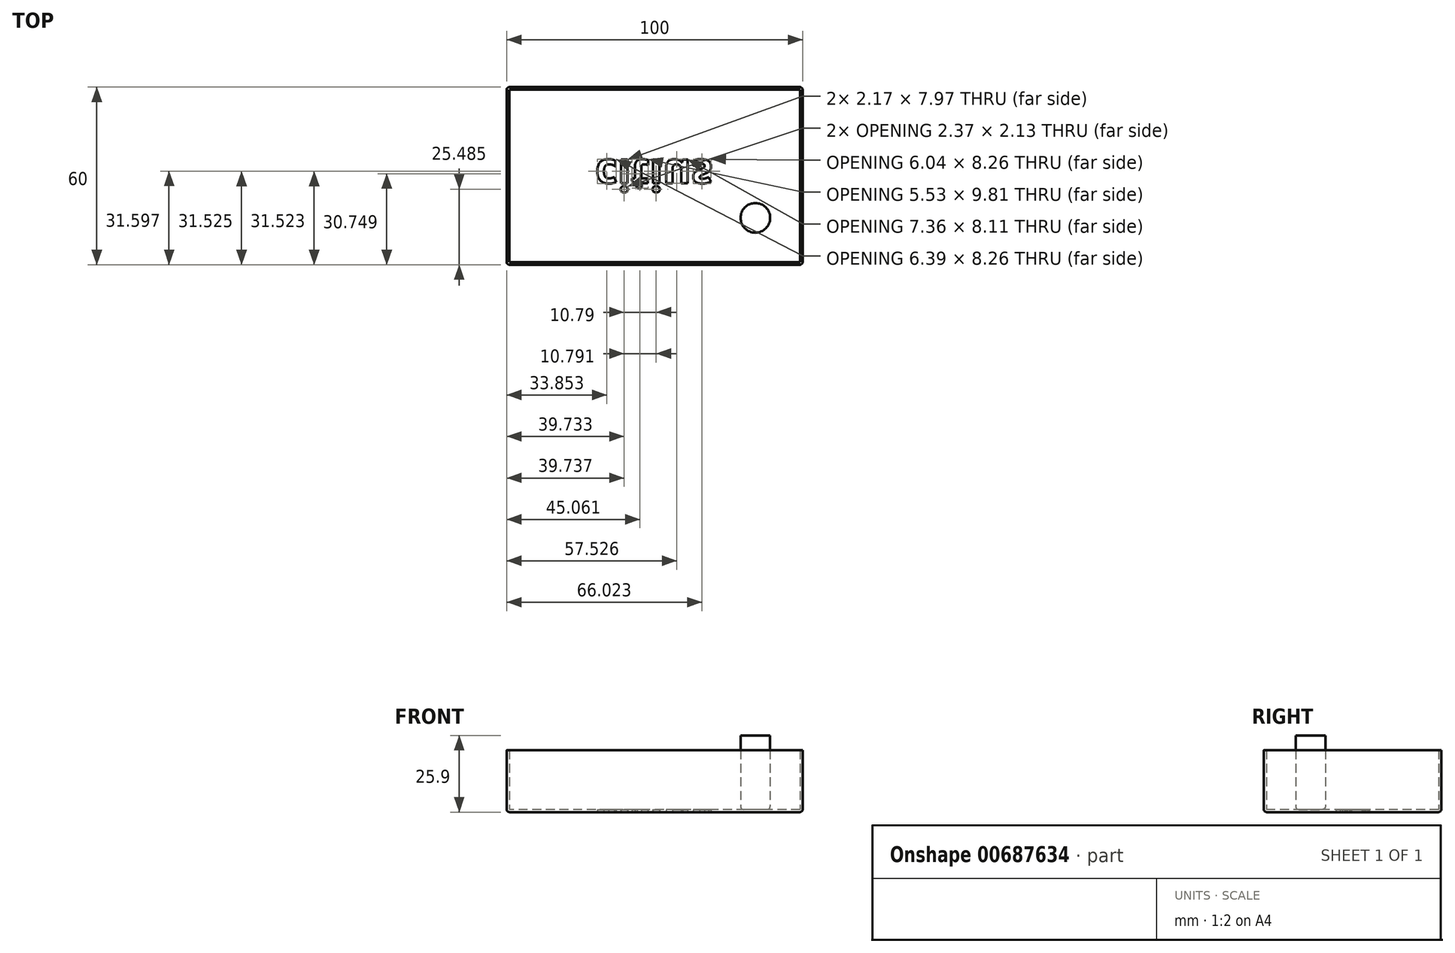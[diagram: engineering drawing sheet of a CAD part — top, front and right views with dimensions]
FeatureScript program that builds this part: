
annotation { "Feature Type Name" : "Feature", "Feature Type Description" : "" }
export const myFeature = defineFeature(function(context is Context, id is Id, definition is map)
    precondition{}
    {
        {
            var Q0;
            Q0=qCreatedBy(makeId("Top.planeOp"),FACE);
            var sketch = newSketch(context, id + "F0", { "sketchPlane" : qUnion([Q0])});
            skLineSegment(sketch, "E0.bottom", {"start": v(-47.64, 21.7) * mm, "end": v(52.36, 21.7) * mm});
            skLineSegment(sketch, "E0.top", {"start": v(-47.64, -38.3) * mm, "end": v(52.36, -38.3) * mm});
            skLineSegment(sketch, "E0.left", {"start": v(-47.64, 21.7) * mm, "end": v(-47.64, -38.3) * mm});
            skLineSegment(sketch, "E0.right", {"start": v(52.36, 21.7) * mm, "end": v(52.36, -38.3) * mm});
            skSolve(sketch);
        }
        {
            var Q0;
            Q0=makeQuery(id+"F0.imprint","IMPRINT",FACE,{"disambiguationData":[TD([[makeQuery(id+"F0.imprint","IMPRINT",EDGE,{"derivedFrom":sQuery(id+"F0.wireOp",EDGE,"E0.bottom")}),-1.0]])]});
            extrude(context, id + "F1", {"entities" : qUnion([Q0]), "depth" : 0.9 * mm, "offsetDistance" : 25 * mm});
        }
        {
            var Q0;
            Q0=makeQuery(id+"F1.opExtrude","CAP_FACE",FACE,{"disambiguationData":[OSD([sQuery(id+"F0.wireOp",EDGE,"E0.bottom"),sQuery(id+"F0.wireOp",EDGE,"E0.top"),sQuery(id+"F0.wireOp",EDGE,"E0.left"),sQuery(id+"F0.wireOp",EDGE,"E0.right")])],"isStart":false});
            var sketch = newSketch(context, id + "F2", { "sketchPlane" : qUnion([Q0])});
            skLineSegment(sketch, "E1.bottom", {"start": v(-47.64, 21.7) * mm, "end": v(-46.74, 21.7) * mm});
            skLineSegment(sketch, "E1.top", {"start": v(-47.64, -38.3) * mm, "end": v(-46.74, -38.3) * mm});
            skLineSegment(sketch, "E1.left", {"start": v(-47.64, 21.7) * mm, "end": v(-47.64, -38.3) * mm});
            skLineSegment(sketch, "E1.right", {"start": v(-46.74, 21.7) * mm, "end": v(-46.74, -38.3) * mm});
            skLineSegment(sketch, "E2.bottom", {"start": v(-46.74, 21.7) * mm, "end": v(52.36, 21.7) * mm});
            skLineSegment(sketch, "E2.top", {"start": v(-46.74, 20.8) * mm, "end": v(52.36, 20.8) * mm});
            skLineSegment(sketch, "E2.left", {"start": v(-46.74, 21.7) * mm, "end": v(-46.74, 20.8) * mm});
            skLineSegment(sketch, "E2.right", {"start": v(52.36, 21.7) * mm, "end": v(52.36, 20.8) * mm});
            skLineSegment(sketch, "E3.bottom", {"start": v(51.46, 20.8) * mm, "end": v(52.36, 20.8) * mm});
            skLineSegment(sketch, "E3.top", {"start": v(51.46, -38.3) * mm, "end": v(52.36, -38.3) * mm});
            skLineSegment(sketch, "E3.left", {"start": v(51.46, 20.8) * mm, "end": v(51.46, -38.3) * mm});
            skLineSegment(sketch, "E3.right", {"start": v(52.36, 20.8) * mm, "end": v(52.36, -38.3) * mm});
            skLineSegment(sketch, "E4.bottom", {"start": v(51.46, -37.4) * mm, "end": v(-46.74, -37.4) * mm});
            skLineSegment(sketch, "E4.top", {"start": v(51.46, -38.3) * mm, "end": v(-46.74, -38.3) * mm});
            skLineSegment(sketch, "E4.left", {"start": v(51.46, -37.4) * mm, "end": v(51.46, -38.3) * mm});
            skLineSegment(sketch, "E4.right", {"start": v(-46.74, -37.4) * mm, "end": v(-46.74, -38.3) * mm});
            skSolve(sketch);
        }
        {
            var Q0;
            Q0 = qSketchRegion(id + "F2", true);
            extrude(context, id + "F3", {"entities" : qUnion([Q0]), "operationType" : NewBodyOperationType.ADD, "depth" : 20 * mm, "offsetDistance" : 25 * mm});
        }
        {
            var Q0;
            Q0=makeQuery(id+"F1.opExtrude","CAP_FACE",FACE,{"disambiguationData":[OSD([sQuery(id+"F0.wireOp",EDGE,"E0.bottom"),sQuery(id+"F0.wireOp",EDGE,"E0.top"),sQuery(id+"F0.wireOp",EDGE,"E0.left"),sQuery(id+"F0.wireOp",EDGE,"E0.right")])],"isStart":true});
            var sketch = newSketch(context, id + "F4", { "sketchPlane" : qUnion([Q0])});
            skText(sketch, "E5", { "text": "citius", "fontName": "OpenSans-Bold.ttf"});
            const initialGuessF4  = {"E5": [-0.01764, 0.0028, 1, 0, 0.01051]};
            skSetInitialGuess(sketch, initialGuessF4);
            skSolve(sketch);
        }
        {
            var Q0;
            Q0 = qSketchRegion(id + "F4", true);
            extrude(context, id + "F5", {"entities" : qUnion([Q0]), "operationType" : NewBodyOperationType.REMOVE, "oppositeDirection" : true, "depth" : 2 * mm, "offsetDistance" : 25 * mm});
        }
        {
            var Q0;
            Q0=makeQuery(id+"F1.opExtrude","CAP_FACE",FACE,{"disambiguationData":[OSD([sQuery(id+"F0.wireOp",EDGE,"E0.bottom"),sQuery(id+"F0.wireOp",EDGE,"E0.top"),sQuery(id+"F0.wireOp",EDGE,"E0.left"),sQuery(id+"F0.wireOp",EDGE,"E0.right")])],"isStart":false});
            var sketch = newSketch(context, id + "F6", { "sketchPlane" : qUnion([Q0])});
            skCircle(sketch, "E6", {"center": v(36.38, -22.49) * mm, "radius": 5 * mm});
            skSolve(sketch);
        }
        {
            var Q0;
            Q0=makeQuery(id+"F6.imprint","IMPRINT",FACE,{"disambiguationData":[TD([[makeQuery(id+"F6.imprint","IMPRINT",EDGE,{"derivedFrom":sQuery(id+"F6.wireOp",EDGE,"E6")}),1.0]])]});
            extrude(context, id + "F7", {"entities" : qUnion([Q0]), "depth" : 25 * mm, "offsetDistance" : 25 * mm});
        }
        {
            var Q0;
            Q0=makeQuery(id+"F3.boolean.opBoolean","MERGE",EDGE,{"derivedFrom":[makeQuery(id+"F1.opExtrude","SWEPT_EDGE",EDGE,{"disambiguationData":[OSD([sQuery(id+"F0.wireOp",EDGE,"E0.bottom"),sQuery(id+"F0.wireOp",EDGE,"E0.right")])]}),makeQuery(id+"F3.opExtrude","SWEPT_EDGE",EDGE,{"disambiguationData":[OSD([sQuery(id+"F2.wireOp",EDGE,"E2.bottom"),sQuery(id+"F2.wireOp",EDGE,"E2.right")])]})]});
            var Q1;
            Q1=makeQuery(id+"F3.boolean.opBoolean","MERGE",EDGE,{"derivedFrom":[makeQuery(id+"F1.opExtrude","SWEPT_EDGE",EDGE,{"disambiguationData":[OSD([sQuery(id+"F0.wireOp",EDGE,"E0.top"),sQuery(id+"F0.wireOp",EDGE,"E0.right")])]}),makeQuery(id+"F3.opExtrude","SWEPT_EDGE",EDGE,{"disambiguationData":[OSD([sQuery(id+"F2.wireOp",EDGE,"E3.top"),sQuery(id+"F2.wireOp",EDGE,"E3.right")])]})]});
            var Q2;
            Q2=makeQuery(id+"F3.boolean.opBoolean","MERGE",EDGE,{"derivedFrom":[makeQuery(id+"F1.opExtrude","SWEPT_EDGE",EDGE,{"disambiguationData":[OSD([sQuery(id+"F0.wireOp",EDGE,"E0.top"),sQuery(id+"F0.wireOp",EDGE,"E0.left")])]}),makeQuery(id+"F3.opExtrude","SWEPT_EDGE",EDGE,{"disambiguationData":[OSD([sQuery(id+"F2.wireOp",EDGE,"E1.top"),sQuery(id+"F2.wireOp",EDGE,"E1.left")])]})]});
            var Q3;
            Q3=makeQuery(id+"F3.boolean.opBoolean","MERGE",EDGE,{"derivedFrom":[makeQuery(id+"F1.opExtrude","SWEPT_EDGE",EDGE,{"disambiguationData":[OSD([sQuery(id+"F0.wireOp",EDGE,"E0.bottom"),sQuery(id+"F0.wireOp",EDGE,"E0.left")])]}),makeQuery(id+"F3.opExtrude","SWEPT_EDGE",EDGE,{"disambiguationData":[OSD([sQuery(id+"F2.wireOp",EDGE,"E1.bottom"),sQuery(id+"F2.wireOp",EDGE,"E1.left")])]})]});
            var Q4;
            Q4=makeQuery(id+"F1.opExtrude","CAP_EDGE",EDGE,{"disambiguationData":[OSD([sQuery(id+"F0.wireOp",EDGE,"E0.bottom")])],"isStart":true});
            var Q5;
            Q5=makeQuery(id+"F1.opExtrude","CAP_EDGE",EDGE,{"disambiguationData":[OSD([sQuery(id+"F0.wireOp",EDGE,"E0.left")])],"isStart":true});
            var Q6;
            Q6=makeQuery(id+"F1.opExtrude","CAP_EDGE",EDGE,{"disambiguationData":[OSD([sQuery(id+"F0.wireOp",EDGE,"E0.top")])],"isStart":true});
            var Q7;
            Q7=makeQuery(id+"F1.opExtrude","CAP_EDGE",EDGE,{"disambiguationData":[OSD([sQuery(id+"F0.wireOp",EDGE,"E0.right")])],"isStart":true});
            var Q8;
            Q8=makeQuery(id+"F7.opExtrude","CAP_EDGE",EDGE,{"disambiguationData":[OSD([sQuery(id+"F6.wireOp",EDGE,"E6")])],"isStart":true});
            fillet(context, id + "F8", {"entities" : qUnion([Q0, Q1, Q2, Q3, Q4, Q5, Q6, Q7, Q8]), "radius" : 1 * mm, "tangentPropagation" : true, "allowEdgeOverflow" : false});
        }
    });
